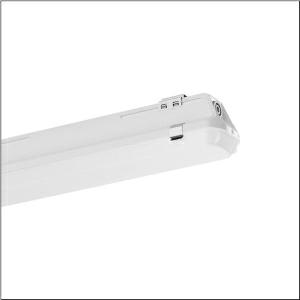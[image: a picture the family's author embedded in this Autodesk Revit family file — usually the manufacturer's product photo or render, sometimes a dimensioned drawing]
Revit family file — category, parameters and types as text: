
# Revit family: monsun_r__21_51fb207p460b005_f6e2
name_source: partatom
category: Lighting Fixtures
units: mm (PartAtom-declared; Revit-internal decimal feet)

## family parameters
Cut with Voids When Loaded = No
Host = Face
Light Source = No
Part Type = Normal
Room Calculation Point = No
Round Connector Dimension = Use Diameter
Shared = No

## types (1)
- Monsun® 21 (1 x LED, 5400 lm, 38 W, 4000K)
    Apparent Load = 38 VA
    CIE Flux Codes = 45 75 93 94 100
    Color Rendering = 80
    Color Temperature = 4000K
    Default Elevation = 1800 mm
    Description = Monsun® 21, damp-proof luminaire, chain hanger, primary optical cover: enclosure, of PC, light emission: direct distribution, primary light characteristic: symmetric, installation type: suspended mounting, surface-mounted, horizontal mounting, vertical mounting, LED, rated luminous flux: 5.400lm, luminous efficacy: 142lm/W, light colour: 840, colour temperature: 4000K, control gear: ECG, with terminal, 3-pole, max. 2.5mm², through-wiring: 5x 2.5mm², mains connection: 220..240V, AC, 50/60Hz, rated input power: 38W, housing, of glass-fibre reinforced polyester, uncoated, bright grey, incl. chain hanger, length: 1.590mm, width: 90mm, height: 88mm, clip for enclosure, of stainless steel (V2A), ceiling mounting element, of stainless steel (V2A), chain hanger, of stainless steel (V2A), protection rating (complete): IP66, insulation class (complete): insulation class I (protective earthing), certification: CE, ENEC, VDE, UKCA, protection symbol: D, impact resistance: IK08, permissible operating ambient temperature: -25..+35°C, standard: EN 50419, EN 60598-2-1, corresponds to IFS (International Featured Standards) requirements for safety and quality in the food industry, for indoor or canopied outdoor use, no direct snow, no direct sun, no direct rain, contact your sales advisor before using the luminaires in applications with unclear chemical exposure, large temperature fluctuations or condensation-forming humidity, LABS conformity tested according to VDMA 24364:2018-05, packaging unit: 1 piece
    Height = 89 mm
    Lamp = 1 x LED
    Lamp Light Flux = 5400 lm
    Lamp Power = 38 W
    Lamp count = 1
    Length = 1590 mm
    Luminous efficacy = 142 lm/W
    Manufacturer = Siteco
    ModVariant = No
    Model = 51FB207P460B005
    Mounting Place = Ceiling
    Mounting Type = Surface mounted
    Number of Poles = 1
    OnlyDefault = Yes
    Power Factor = 1
    Product Name = Monsun® 21
    Product group = damp-proof luminaire
    ProductGroupID = 301
    Protection Class = Protection class I
    Protection Degree = IP 66
    RLX_Detail_Level = 1
    RLX_Emergency_Light_Flux = 0 lm
    RLX_Emergency_Type = 0
    RLX_Emergency_Type_DB = No
    RlxData = <blob elided: 88957 chars, md5=1061ba6c>
    Socket = socket
    Standby Power = 0 W
    System Light Flux = 5400 lm
    System Power = 38 W
    Type Comments = Product without accessories
    Type Image = l_1006717.jpg
    URL = http://relux.com
    VarID = ---
    Voltage = 0 V
    Weight = 0.00 kg
    Width = 90 mm

## geometry (parser evidence)
native form markers: Blend x4, Sweep x13
no freeform markers — native parametric forms only
